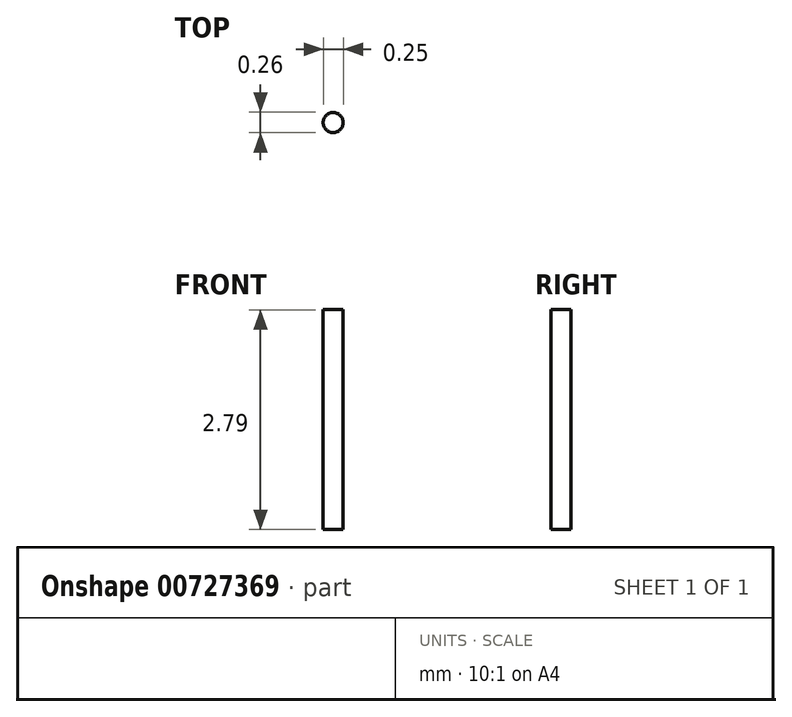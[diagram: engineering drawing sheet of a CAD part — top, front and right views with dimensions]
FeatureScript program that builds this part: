
annotation { "Feature Type Name" : "Feature", "Feature Type Description" : "" }
export const myFeature = defineFeature(function(context is Context, id is Id, definition is map)
    precondition{}
    {
        {
            var Q0;
            Q0=qCreatedBy(makeId("Top.planeOp"),FACE);
            var sketch = newSketch(context, id + "F0", { "sketchPlane" : qUnion([Q0])});
            skCircle(sketch, "E0", {"center": v(-66.75, -47.73) * mm, "radius": 0.13 * mm});
            skSolve(sketch);
        }
        {
            var Q0;
            Q0=makeQuery(id+"F0.imprint","IMPRINT",FACE,{"disambiguationData":[TD([[makeQuery(id+"F0.imprint","IMPRINT",EDGE,{"derivedFrom":sQuery(id+"F0.wireOp",EDGE,"E0")}),1.0]])]});
            extrude(context, id + "F1", {"entities" : qUnion([Q0]), "depth" : 2.8 * mm, "offsetDistance" : 25.4 * mm});
        }
    });
